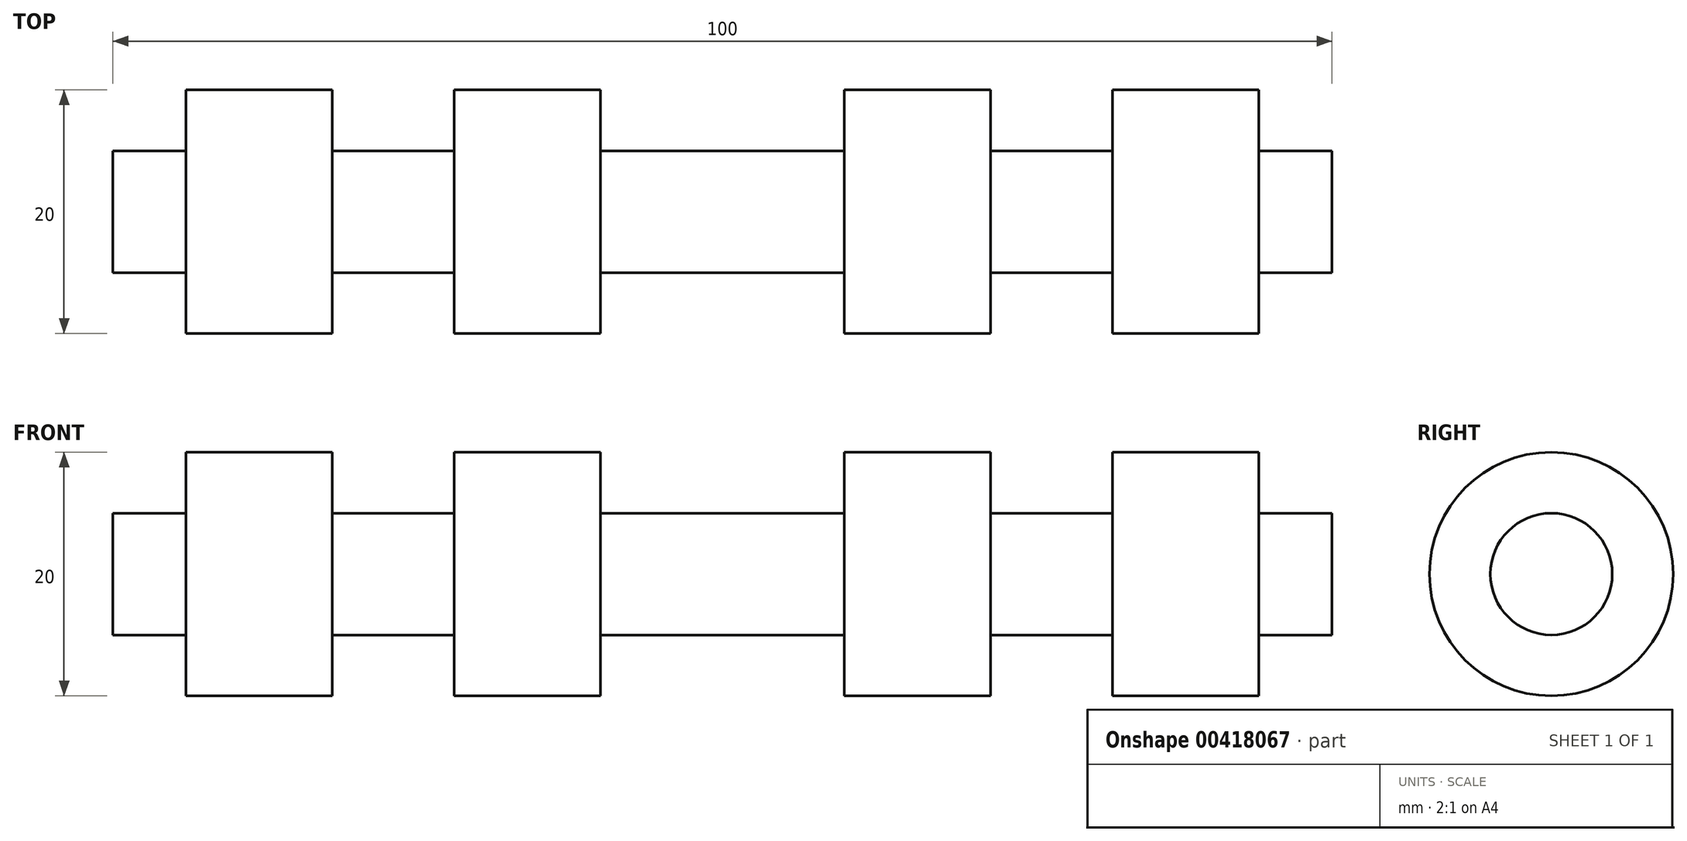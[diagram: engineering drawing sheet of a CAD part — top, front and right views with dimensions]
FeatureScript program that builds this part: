
annotation { "Feature Type Name" : "Feature", "Feature Type Description" : "" }
export const myFeature = defineFeature(function(context is Context, id is Id, definition is map)
    precondition{}
    {
        {
            var Q0;
            Q0=qCreatedBy(makeId("Front.planeOp"),FACE);
            var sketch = newSketch(context, id + "F0", { "sketchPlane" : qUnion([Q0])});
            skLineSegment(sketch, "E0.bottom", {"start": v(0, 0) * mm, "end": v(-100, 0) * mm});
            skLineSegment(sketch, "E0.top", {"start": v(-6, 10) * mm, "end": v(-18, 10) * mm});
            skLineSegment(sketch, "E0.left", {"start": v(0, 0) * mm, "end": v(0, 5) * mm});
            skLineSegment(sketch, "E0.right", {"start": v(-100, 0) * mm, "end": v(-100, 5) * mm});
            skLineSegment(sketch, "E1", {"start": v(-100, 5) * mm, "end": v(-94, 5) * mm});
            skLineSegment(sketch, "E2", {"start": v(-94, 10) * mm, "end": v(-94, 5) * mm});
            skLineSegment(sketch, "E3", {"start": v(-6, 10) * mm, "end": v(-6, 5) * mm});
            skLineSegment(sketch, "E4", {"start": v(-82, 10) * mm, "end": v(-82, 5) * mm});
            skLineSegment(sketch, "E5", {"start": v(-72, 10) * mm, "end": v(-72, 5) * mm});
            skLineSegment(sketch, "E6", {"start": v(-28, 10) * mm, "end": v(-28, 5) * mm});
            skLineSegment(sketch, "E7", {"start": v(-18, 10) * mm, "end": v(-18, 5) * mm});
            skLineSegment(sketch, "E8.trimOffspring", {"start": v(-6, 5) * mm, "end": v(0, 5) * mm});
            skLineSegment(sketch, "E9.trimOffspring", {"start": v(-28, 10) * mm, "end": v(-40, 10) * mm});
            skPoint(sketch, "E10.orphan", {"position": v(-18, 3.18) * mm});
            skPoint(sketch, "E11.orphan", {"position": v(-28, 3.18) * mm});
            skLineSegment(sketch, "E12.trimOffspring", {"start": v(-28, 5) * mm, "end": v(-18, 5) * mm});
            skPoint(sketch, "E13.orphan", {"position": v(-72, 3.18) * mm});
            skPoint(sketch, "E14.orphan", {"position": v(-82, 3.18) * mm});
            skLineSegment(sketch, "E15.trimOffspring", {"start": v(-82, 10) * mm, "end": v(-94, 10) * mm});
            skLineSegment(sketch, "E16.trimOffspring", {"start": v(-82, 5) * mm, "end": v(-72, 5) * mm});
            skLineSegment(sketch, "E17", {"start": v(13.67, 0) * mm, "end": v(-102.29, 0) * mm, "construction": true});
            skLineSegment(sketch, "E18", {"start": v(-60, 10) * mm, "end": v(-60, 5) * mm});
            skLineSegment(sketch, "E19", {"start": v(-40, 10) * mm, "end": v(-40, 5) * mm});
            skLineSegment(sketch, "E20.trimOffspring", {"start": v(-60, 10) * mm, "end": v(-72, 10) * mm});
            skLineSegment(sketch, "E21", {"start": v(-60, 5) * mm, "end": v(-40, 5) * mm});
            skSolve(sketch);
        }
        {
            var Q0;
            Q0 = qSketchRegion(id + "F0", true);
            var Q1;
            Q1=sQuery(id+"F0.wireOp",EDGE,"E17");
            revolve(context, id + "F1", {"surfaceOperationType" : NewSurfaceOperationType.NEW, "entities" : qUnion([Q0]), "axis" : qUnion([Q1]), "revolveType" : RevolveType.FULL});
        }
    });
